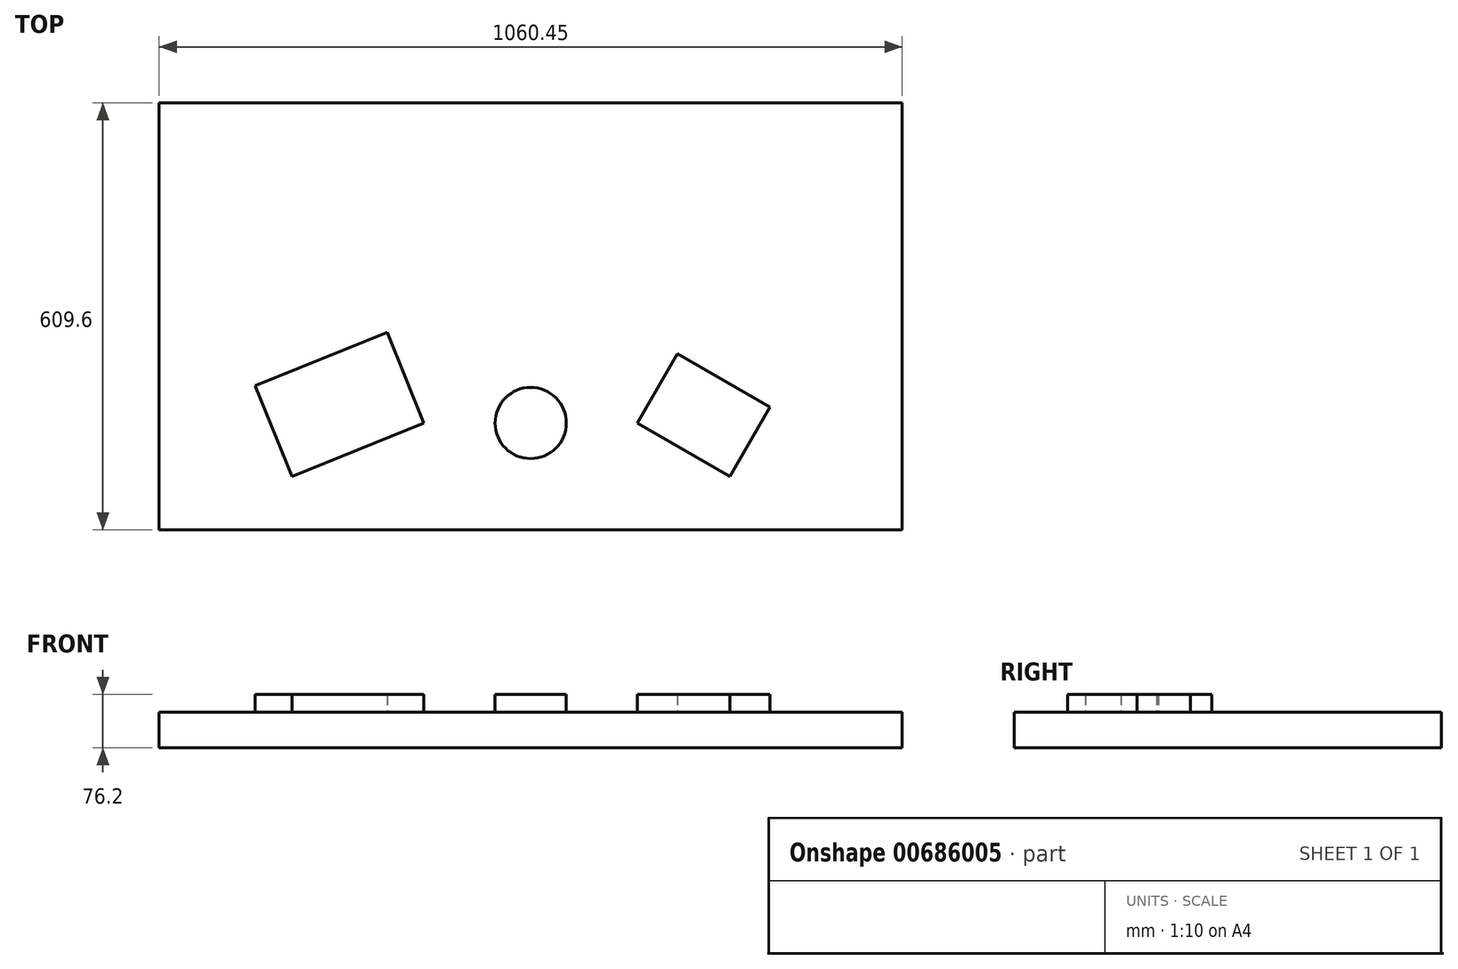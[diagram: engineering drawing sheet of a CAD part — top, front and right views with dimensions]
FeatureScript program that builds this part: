
annotation { "Feature Type Name" : "Feature", "Feature Type Description" : "" }
export const myFeature = defineFeature(function(context is Context, id is Id, definition is map)
    precondition{}
    {
        {
            var Q0;
            Q0=qCreatedBy(makeId("Top.planeOp"),FACE);
            var sketch = newSketch(context, id + "F0", { "sketchPlane" : qUnion([Q0])});
            skLineSegment(sketch, "E0.bottom", {"start": v(0, 0) * mm, "end": v(1060.45, 0) * mm});
            skLineSegment(sketch, "E0.top", {"start": v(0, 609.6) * mm, "end": v(1060.45, 609.6) * mm});
            skLineSegment(sketch, "E0.left", {"start": v(0, 0) * mm, "end": v(0, 609.6) * mm});
            skLineSegment(sketch, "E0.right", {"start": v(1060.45, 0) * mm, "end": v(1060.45, 609.6) * mm});
            skPoint(sketch, "E1", {"position": v(530.22, 0) * mm});
            skPoint(sketch, "E2", {"position": v(1060.45, 128.69) * mm});
            skPoint(sketch, "E3", {"position": v(1060.45, 306.49) * mm});
            skSolve(sketch);
        }
        {
            var Q0;
            Q0=makeQuery(id+"F0.imprint","IMPRINT",FACE,{"disambiguationData":[TD([[makeQuery(id+"F0.imprint","IMPRINT",EDGE,{"derivedFrom":sQuery(id+"F0.wireOp",EDGE,"E0.bottom")}),1.0]])]});
            var sketch = newSketch(context, id + "F1", { "sketchPlane" : qUnion([Q0])});
            skPoint(sketch, "E4", {"position": v(137.07, 205.7) * mm});
            skPoint(sketch, "E5", {"position": v(189.45, 76.2) * mm});
            skPoint(sketch, "E6", {"position": v(377.82, 152.4) * mm});
            skPoint(sketch, "E7", {"position": v(325.44, 281.9) * mm});
            skLineSegment(sketch, "E8", {"start": v(325.44, 281.9) * mm, "end": v(377.82, 152.4) * mm});
            skLineSegment(sketch, "E9", {"start": v(189.45, 76.2) * mm, "end": v(377.82, 152.4) * mm});
            skLineSegment(sketch, "E10", {"start": v(137.07, 205.7) * mm, "end": v(325.44, 281.9) * mm});
            skLineSegment(sketch, "E11", {"start": v(137.07, 205.7) * mm, "end": v(189.45, 76.2) * mm});
            skPoint(sketch, "E12", {"position": v(739.78, 251.39) * mm});
            skPoint(sketch, "E13", {"position": v(682.62, 152.4) * mm});
            skPoint(sketch, "E14", {"position": v(814.6, 76.2) * mm});
            skPoint(sketch, "E15", {"position": v(871.76, 175.19) * mm});
            skLineSegment(sketch, "E16", {"start": v(871.76, 175.19) * mm, "end": v(814.6, 76.2) * mm});
            skLineSegment(sketch, "E17", {"start": v(682.62, 152.4) * mm, "end": v(814.6, 76.2) * mm});
            skLineSegment(sketch, "E18", {"start": v(739.78, 251.39) * mm, "end": v(871.76, 175.19) * mm});
            skLineSegment(sketch, "E19", {"start": v(739.77, 251.39) * mm, "end": v(682.62, 152.4) * mm});
            skPoint(sketch, "E20", {"position": v(530.22, 152.4) * mm});
            skCircle(sketch, "E21", {"center": v(530.22, 152.4) * mm, "radius": 50.8 * mm});
            skSolve(sketch);
        }
        {
            var Q0;
            Q0=qSketchRegion(id+"F0",true);
            extrude(context, id + "F2", {"entities" : qUnion([Q0]), "oppositeDirection" : true, "depth" : 50.8 * mm, "offsetDistance" : 25.4 * mm});
        }
        {
            var Q0;
            Q0=qSketchRegion(id+"F1",true);
            extrude(context, id + "F3", {"entities" : qUnion([Q0]), "operationType" : NewBodyOperationType.ADD, "depth" : 25.4 * mm, "offsetDistance" : 25.4 * mm});
        }
    });
